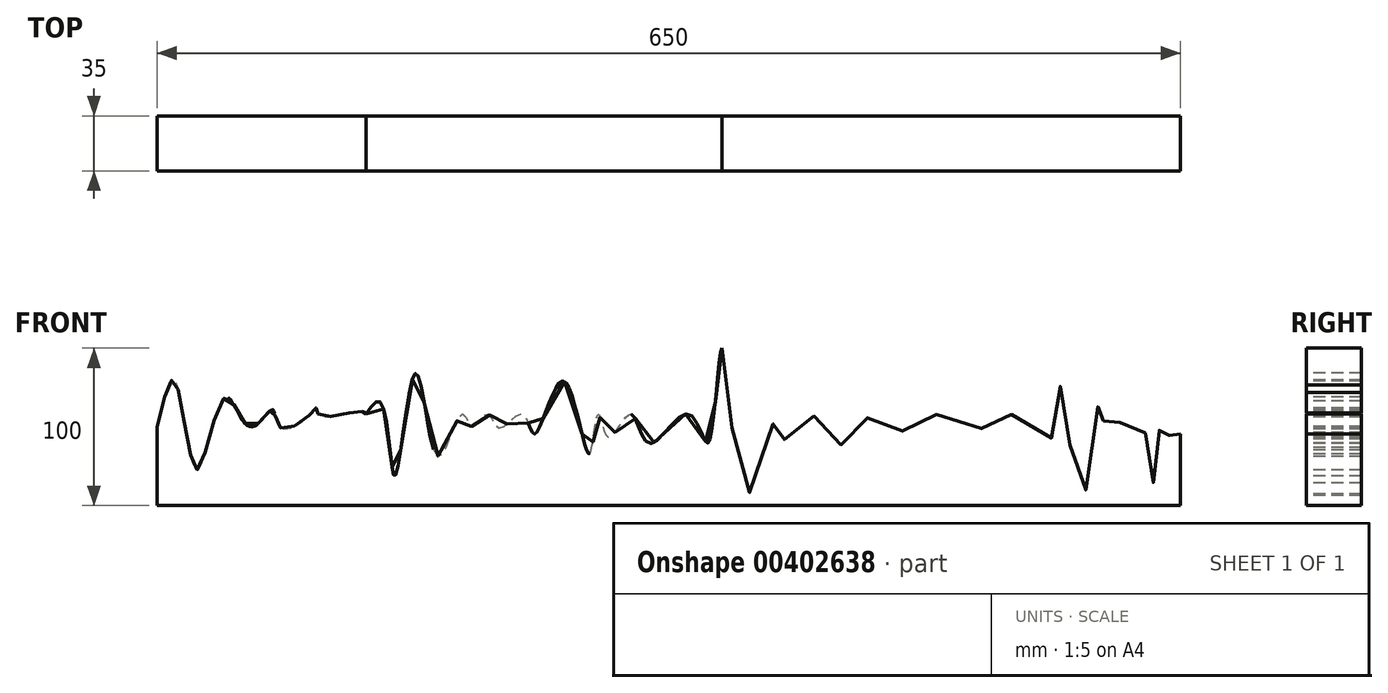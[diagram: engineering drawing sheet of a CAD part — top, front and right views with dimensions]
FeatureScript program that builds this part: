
annotation { "Feature Type Name" : "Feature", "Feature Type Description" : "" }
export const myFeature = defineFeature(function(context is Context, id is Id, definition is map)
    precondition{}
    {
        {
            var Q0;
            Q0=qCreatedBy(makeId("Front.planeOp"),FACE);
            var sketch = newSketch(context, id + "F0", { "sketchPlane" : qUnion([Q0])});
            skLineSegment(sketch, "E0.bottom", {"start": v(-209.99, 77.36) * mm, "end": v(440.01, 77.36) * mm});
            skLineSegment(sketch, "E0.top", {"start": v(-209.99, -22.64) * mm, "end": v(440.01, -22.64) * mm});
            skLineSegment(sketch, "E0.left", {"start": v(-209.99, 77.36) * mm, "end": v(-209.99, -22.64) * mm});
            skLineSegment(sketch, "E0.right", {"start": v(440.01, 77.36) * mm, "end": v(440.01, -22.64) * mm});
            skSolve(sketch);
        }
        {
            var Q0;
            Q0=makeQuery(id+"F0.imprint","IMPRINT",FACE,{"disambiguationData":[TD([[makeQuery(id+"F0.imprint","IMPRINT",EDGE,{"derivedFrom":sQuery(id+"F0.wireOp",EDGE,"E0.bottom")}),-1.0]])]});
            extrude(context, id + "F1", {"entities" : qUnion([Q0]), "depth" : 35 * mm});
        }
        {
            var Q0;
            Q0=makeQuery(id+"F1.opExtrude","CAP_FACE",FACE,{"disambiguationData":[OSD([sQuery(id+"F0.wireOp",EDGE,"E0.bottom"),sQuery(id+"F0.wireOp",EDGE,"E0.top"),sQuery(id+"F0.wireOp",EDGE,"E0.left"),sQuery(id+"F0.wireOp",EDGE,"E0.right")])],"isStart":false});
            var sketch = newSketch(context, id + "F2", { "sketchPlane" : qUnion([Q0])});
            skLineSegment(sketch, "E1", {"start": v(-209.99, -22.64) * mm, "end": v(-252, -22.64) * mm});
            skLineSegment(sketch, "E2", {"start": v(-252, -22.64) * mm, "end": v(-252, 27.36) * mm});
            skLineSegment(sketch, "E3", {"start": v(-252, 27.36) * mm, "end": v(-209.99, 27.36) * mm});
            skFitSpline(sketch, "E4", {"points": [v(-209.99, 27.36) * mm, v(-198.48, 56.24) * mm, v(-184.46, 0) * mm, v(-166.5, 46.14) * mm, v(-150.79, 27.36) * mm, v(-136.76, 38.29) * mm, v(-132.27, 27.36) * mm, v(-114.87, 33.24) * mm, v(-108.7, 39.4) * mm, v(-107.02, 34.92) * mm, v(-85.13, 36.6) * mm, v(-77.83, 36.6) * mm, v(-77.27, 35.48) * mm], "startDerivative": vector(109.27, 468.51) * mm, "endDerivative": vector(13.4, -56.38) * mm});
            skFitSpline(sketch, "E5", {"points": [v(-77.27, 35.48) * mm, v(-67.6, 42.6) * mm, v(-58.9, -3.83) * mm, v(-45.47, 61.57) * mm, v(-31.32, 8.72) * mm, v(-16.22, 35.48) * mm, v(-9.61, 27.6) * mm, v(0, 35.48) * mm, v(7.38, 26.65) * mm, v(22, 35.48) * mm, v(30.03, 22.88) * mm, v(47.96, 56.38) * mm, v(64.47, 10.14) * mm, v(70.14, 35.48) * mm, v(76.74, 20.99) * mm, v(90.9, 35.48) * mm, v(102.7, 16.74) * mm, v(127.7, 35.48) * mm, v(139.97, 17.21) * mm, v(148.94, 77.36) * mm, v(164.51, -15.35) * mm, v(184.33, 35.48) * mm, v(190, 17.21) * mm, v(210.76, 35.48) * mm, v(226.8, 14.38) * mm, v(244.73, 35.48) * mm, v(266.44, 23.82) * mm, v(286.73, 35.48) * mm, v(317.4, 26.18) * mm, v(331.56, 35.48) * mm, v(358.45, 20.52) * mm, v(364.12, 54.02) * mm, v(377.8, -16.29) * mm, v(389.13, 49.3) * mm, v(393.85, 20.05) * mm, v(406.11, 35.48) * mm, v(420.27, 13.91) * mm, v(423.1, -7.8) * mm, v(429.24, 35.48) * mm, v(435.37, 12.97) * mm, v(440.01, 22.88) * mm], "startDerivative": vector(673.78, 1000.22) * mm, "endDerivative": vector(311.72, 1177.85) * mm});
            skLineSegment(sketch, "E6", {"start": v(-209.99, 27.36) * mm, "end": v(-209.99, 77.36) * mm});
            skLineSegment(sketch, "E7", {"start": v(-209.99, 77.36) * mm, "end": v(440.01, 77.36) * mm});
            skLineSegment(sketch, "E8", {"start": v(440.01, 77.36) * mm, "end": v(440.01, 22.88) * mm});
            skSolve(sketch);
        }
        {
            var Q0;
            {var subQ0=sQuery(id+"F2.wireOp",EDGE,"E4");Q0=makeQuery(id+"F2.imprint","IMPRINT",FACE,{"disambiguationData":[TD([[makeQuery(id+"F2.imprint","IMPRINT",EDGE,{"derivedFrom":subQ0}),1.0]])]});}
            var Q1;
            {var subQ0=sQuery(id+"F2.wireOp",EDGE,"E8");Q1=makeQuery(id+"F2.imprint","IMPRINT",FACE,{"disambiguationData":[TD([[makeQuery(id+"F2.imprint","IMPRINT",EDGE,{"derivedFrom":subQ0}),-1.0]])]});}
            extrude(context, id + "F3", {"entities" : qUnion([Q0, Q1]), "operationType" : NewBodyOperationType.REMOVE, "endBound" : BoundingType.THROUGH_ALL, "oppositeDirection" : true, "depth" : 25 * mm});
        }
    });
